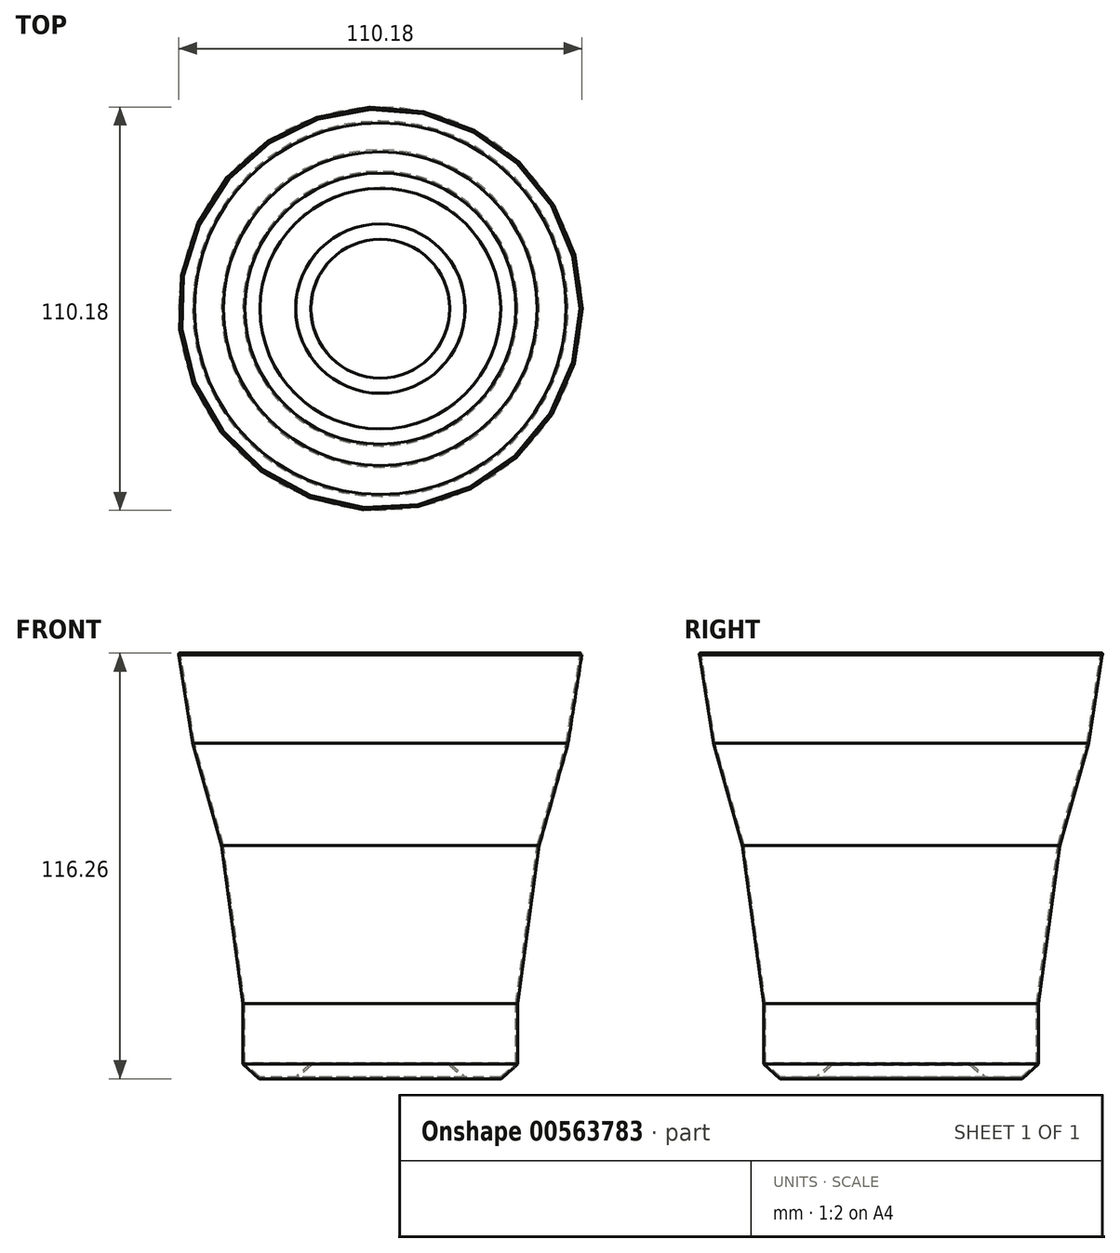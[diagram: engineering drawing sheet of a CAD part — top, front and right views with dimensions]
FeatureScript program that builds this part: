
annotation { "Feature Type Name" : "Feature", "Feature Type Description" : "" }
export const myFeature = defineFeature(function(context is Context, id is Id, definition is map)
    precondition{}
    {
        {
            var Q0;
            Q0=qCreatedBy(makeId("Front.planeOp"),FACE);
            var sketch = newSketch(context, id + "F0", { "sketchPlane" : qUnion([Q0])});
            skLineSegment(sketch, "E0", {"start": v(0, -28.74) * mm, "end": v(18.97, -28.74) * mm});
            skLineSegment(sketch, "E1", {"start": v(18.97, -28.74) * mm, "end": v(23.13, -32.48) * mm});
            skLineSegment(sketch, "E2", {"start": v(23.13, -32.48) * mm, "end": v(32.87, -32.48) * mm});
            skLineSegment(sketch, "E3", {"start": v(32.87, -32.48) * mm, "end": v(37.03, -28.74) * mm});
            skLineSegment(sketch, "E4", {"start": v(37.03, -28.74) * mm, "end": v(37.03, -12.49) * mm});
            skLineSegment(sketch, "E5", {"start": v(37.03, -12.49) * mm, "end": v(42.86, 30.82) * mm});
            skLineSegment(sketch, "E6", {"start": v(42.86, 30.82) * mm, "end": v(50.77, 58.71) * mm});
            skLineSegment(sketch, "E7", {"start": v(50.77, 58.71) * mm, "end": v(54.52, 82.86) * mm});
            skLineSegment(sketch, "E8.0", {"start": v(51.27, 58.6) * mm, "end": v(55.02, 82.78) * mm});
            skLineSegment(sketch, "E8.1", {"start": v(43.36, 30.71) * mm, "end": v(51.27, 58.6) * mm});
            skLineSegment(sketch, "E8.2", {"start": v(37.54, -12.52) * mm, "end": v(43.36, 30.71) * mm});
            skLineSegment(sketch, "E8.3", {"start": v(37.54, -28.96) * mm, "end": v(37.54, -12.52) * mm});
            skLineSegment(sketch, "E8.4", {"start": v(0, -29.24) * mm, "end": v(18.77, -29.24) * mm});
            skLineSegment(sketch, "E8.5", {"start": v(18.77, -29.24) * mm, "end": v(22.94, -33) * mm});
            skLineSegment(sketch, "E8.6", {"start": v(22.94, -33) * mm, "end": v(33.06, -33) * mm});
            skLineSegment(sketch, "E8.7", {"start": v(33.06, -33) * mm, "end": v(37.54, -28.96) * mm});
            skArc(sketch, "E9", {"start": v(55.02, 82.78) * mm, "mid": v(54.84, 83.27) * mm, "end": v(54.52, 82.86) * mm});
            skLineSegment(sketch, "E10", {"start": v(0, -28.74) * mm, "end": v(0, -29.24) * mm});
            skSolve(sketch);
        }
        {
            var Q0;
            Q0=makeQuery(id+"F0.imprint","IMPRINT",FACE,{"disambiguationData":[TD([[makeQuery(id+"F0.imprint","IMPRINT",EDGE,{"derivedFrom":sQuery(id+"F0.wireOp",EDGE,"E0")}),-1.0]])]});
            var Q1;
            Q1=sQuery(id+"F0.wireOp",EDGE,"E10");
            revolve(context, id + "F1", {"entities" : qUnion([Q0]), "axis" : qUnion([Q1]), "revolveType" : RevolveType.FULL});
        }
    });
